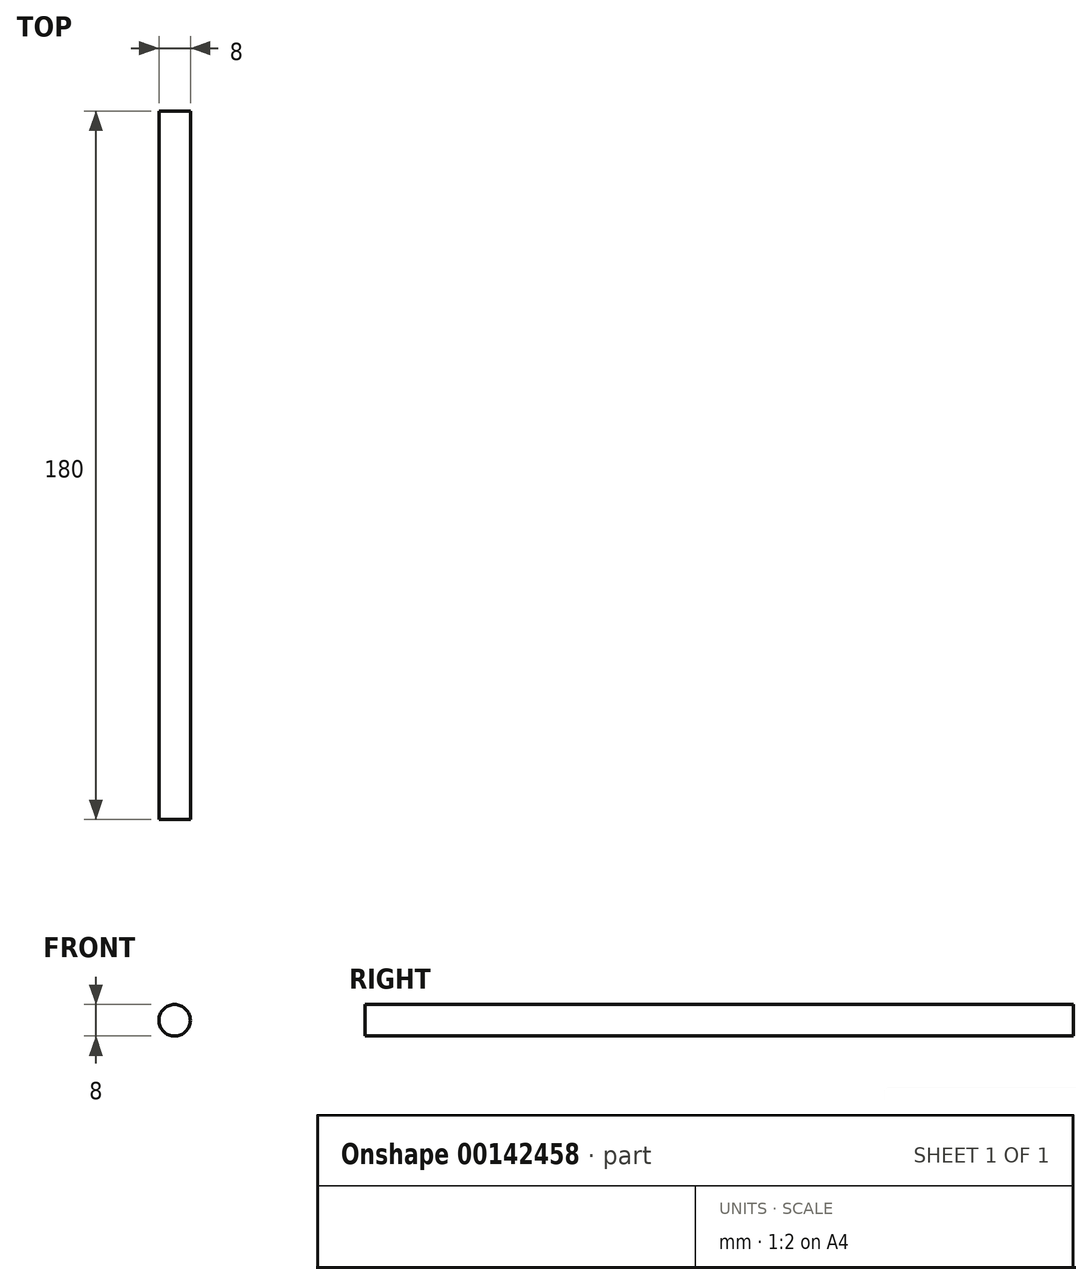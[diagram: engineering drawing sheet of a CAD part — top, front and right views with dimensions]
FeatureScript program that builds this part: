
annotation { "Feature Type Name" : "Feature", "Feature Type Description" : "" }
export const myFeature = defineFeature(function(context is Context, id is Id, definition is map)
    precondition{}
    {
        {
            var Q0;
            Q0=qCreatedBy(makeId("Front.planeOp"),FACE);
            var sketch = newSketch(context, id + "F0", { "sketchPlane" : qUnion([Q0])});
            skCircle(sketch, "E0", {"center": v(0, 0) * mm, "radius": 4 * mm});
            skSolve(sketch);
        }
        {
            var Q0;
            Q0 = qSketchRegion(id + "F0", true);
            extrude(context, id + "F1", {"entities" : qUnion([Q0]), "endBound" : BoundingType.SYMMETRIC, "depth" : 180 * mm});
        }
    });
